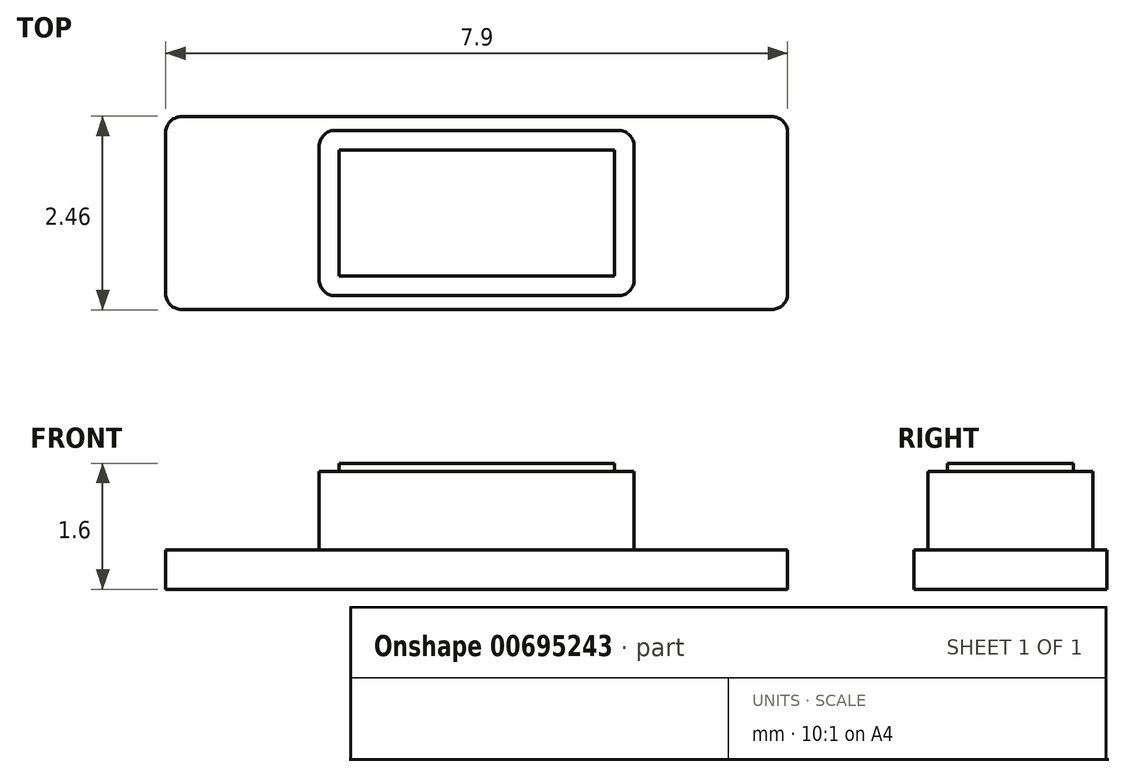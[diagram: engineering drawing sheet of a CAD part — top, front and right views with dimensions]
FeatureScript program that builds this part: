
annotation { "Feature Type Name" : "Feature", "Feature Type Description" : "" }
export const myFeature = defineFeature(function(context is Context, id is Id, definition is map)
    precondition{}
    {
        {
            var Q0;
            Q0=qCreatedBy(makeId("Top.planeOp"),FACE);
            var sketch = newSketch(context, id + "F0", { "sketchPlane" : qUnion([Q0])});
            skLineSegment(sketch, "E0.bottom", {"start": v(3.95, -1.22) * mm, "end": v(-3.95, -1.22) * mm});
            skLineSegment(sketch, "E0.top", {"start": v(3.95, 1.23) * mm, "end": v(-3.95, 1.23) * mm});
            skLineSegment(sketch, "E0.left", {"start": v(3.95, -1.22) * mm, "end": v(3.95, 1.23) * mm});
            skLineSegment(sketch, "E0.right", {"start": v(-3.95, -1.22) * mm, "end": v(-3.95, 1.23) * mm});
            skPoint(sketch, "E0.middle", {"position": v(0, 0) * mm});
            skSolve(sketch);
        }
        {
            var Q0;
            Q0 = qSketchRegion(id + "F0", true);
            extrude(context, id + "F1", {"entities" : qUnion([Q0]), "depth" : 0.5 * mm, "offsetDistance" : 25 * mm});
        }
        {
            var Q0;
            Q0=makeQuery(id+"F1.opExtrude","SWEPT_EDGE",EDGE,{"disambiguationData":[OSD([sQuery(id+"F0.wireOp",EDGE,"E0.bottom"),sQuery(id+"F0.wireOp",EDGE,"E0.right")])]});
            var Q1;
            Q1=makeQuery(id+"F1.opExtrude","SWEPT_EDGE",EDGE,{"disambiguationData":[OSD([sQuery(id+"F0.wireOp",EDGE,"E0.bottom"),sQuery(id+"F0.wireOp",EDGE,"E0.left")])]});
            var Q2;
            Q2=makeQuery(id+"F1.opExtrude","SWEPT_EDGE",EDGE,{"disambiguationData":[OSD([sQuery(id+"F0.wireOp",EDGE,"E0.top"),sQuery(id+"F0.wireOp",EDGE,"E0.left")])]});
            var Q3;
            Q3=makeQuery(id+"F1.opExtrude","SWEPT_EDGE",EDGE,{"disambiguationData":[OSD([sQuery(id+"F0.wireOp",EDGE,"E0.top"),sQuery(id+"F0.wireOp",EDGE,"E0.right")])]});
            fillet(context, id + "F2", {"entities" : qUnion([Q0, Q1, Q2, Q3]), "radius" : 0.2 * mm, "tangentPropagation" : true, "allowEdgeOverflow" : false});
        }
        {
            var Q0;
            Q0=makeQuery(id+"F1.opExtrude","CAP_FACE",FACE,{"disambiguationData":[OSD([sQuery(id+"F0.wireOp",EDGE,"E0.bottom"),sQuery(id+"F0.wireOp",EDGE,"E0.top"),sQuery(id+"F0.wireOp",EDGE,"E0.left"),sQuery(id+"F0.wireOp",EDGE,"E0.right")])],"isStart":false});
            var sketch = newSketch(context, id + "F3", { "sketchPlane" : qUnion([Q0])});
            skLineSegment(sketch, "E1.bottom", {"start": v(2, -1.05) * mm, "end": v(-2, -1.05) * mm});
            skLineSegment(sketch, "E1.top", {"start": v(2, 1.05) * mm, "end": v(-2, 1.05) * mm});
            skLineSegment(sketch, "E1.left", {"start": v(2, -1.05) * mm, "end": v(2, 1.05) * mm});
            skLineSegment(sketch, "E1.right", {"start": v(-2, -1.05) * mm, "end": v(-2, 1.05) * mm});
            skPoint(sketch, "E1.middle", {"position": v(0, 0) * mm});
            skSolve(sketch);
        }
        {
            var Q0;
            Q0 = qSketchRegion(id + "F3", true);
            extrude(context, id + "F4", {"entities" : qUnion([Q0]), "operationType" : NewBodyOperationType.ADD, "depth" : 1 * mm, "offsetDistance" : 25 * mm});
        }
        {
            var Q0;
            Q0=makeQuery(id+"F4.opExtrude","SWEPT_EDGE",EDGE,{"disambiguationData":[OSD([sQuery(id+"F3.wireOp",EDGE,"E1.bottom"),sQuery(id+"F3.wireOp",EDGE,"E1.right")])]});
            var Q1;
            Q1=makeQuery(id+"F4.opExtrude","SWEPT_EDGE",EDGE,{"disambiguationData":[OSD([sQuery(id+"F3.wireOp",EDGE,"E1.bottom"),sQuery(id+"F3.wireOp",EDGE,"E1.left")])]});
            var Q2;
            Q2=makeQuery(id+"F4.opExtrude","SWEPT_EDGE",EDGE,{"disambiguationData":[OSD([sQuery(id+"F3.wireOp",EDGE,"E1.top"),sQuery(id+"F3.wireOp",EDGE,"E1.left")])]});
            var Q3;
            Q3=makeQuery(id+"F4.opExtrude","SWEPT_EDGE",EDGE,{"disambiguationData":[OSD([sQuery(id+"F3.wireOp",EDGE,"E1.top"),sQuery(id+"F3.wireOp",EDGE,"E1.right")])]});
            fillet(context, id + "F5", {"entities" : qUnion([Q0, Q1, Q2, Q3]), "radius" : 0.2 * mm, "tangentPropagation" : true, "allowEdgeOverflow" : false});
        }
        {
            var Q0;
            Q0=makeQuery(id+"F4.opExtrude","CAP_FACE",FACE,{"disambiguationData":[OSD([sQuery(id+"F3.wireOp",EDGE,"E1.bottom"),sQuery(id+"F3.wireOp",EDGE,"E1.top"),sQuery(id+"F3.wireOp",EDGE,"E1.left"),sQuery(id+"F3.wireOp",EDGE,"E1.right")])],"isStart":false});
            var sketch = newSketch(context, id + "F6", { "sketchPlane" : qUnion([Q0])});
            skLineSegment(sketch, "E2.bottom", {"start": v(1.75, -0.8) * mm, "end": v(-1.75, -0.8) * mm});
            skLineSegment(sketch, "E2.top", {"start": v(1.75, 0.8) * mm, "end": v(-1.75, 0.8) * mm});
            skLineSegment(sketch, "E2.left", {"start": v(1.75, -0.8) * mm, "end": v(1.75, 0.8) * mm});
            skLineSegment(sketch, "E2.right", {"start": v(-1.75, -0.8) * mm, "end": v(-1.75, 0.8) * mm});
            skPoint(sketch, "E2.middle", {"position": v(0, 0) * mm});
            skSolve(sketch);
        }
        {
            var Q0;
            Q0 = qSketchRegion(id + "F6", true);
            extrude(context, id + "F7", {"entities" : qUnion([Q0]), "operationType" : NewBodyOperationType.ADD, "depth" : 0.1 * mm, "offsetDistance" : 25 * mm});
        }
    });
